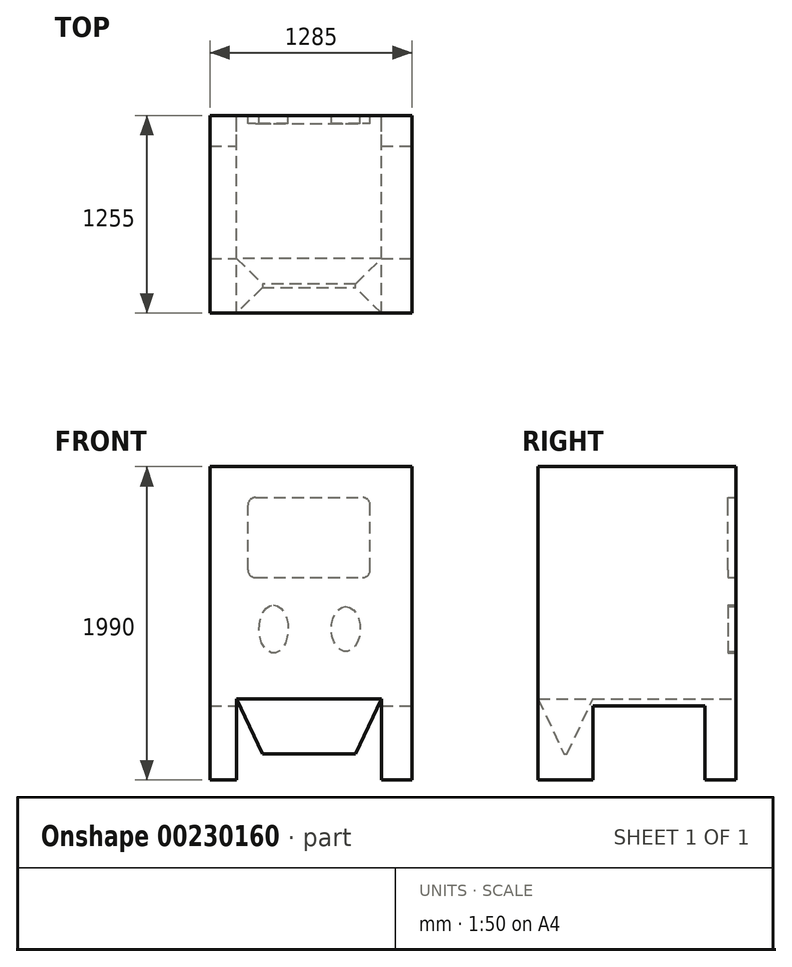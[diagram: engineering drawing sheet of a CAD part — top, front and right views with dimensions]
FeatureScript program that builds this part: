
annotation { "Feature Type Name" : "Feature", "Feature Type Description" : "" }
export const myFeature = defineFeature(function(context is Context, id is Id, definition is map)
    precondition{}
    {
        {
            var Q0;
            Q0=qCreatedBy(makeId("Top.planeOp"),FACE);
            var sketch = newSketch(context, id + "F0", { "sketchPlane" : qUnion([Q0])});
            skLineSegment(sketch, "E0.bottom", {"start": v(630, 615) * mm, "end": v(-630, 615) * mm});
            skLineSegment(sketch, "E0.top", {"start": v(630, -615) * mm, "end": v(-630, -615) * mm});
            skLineSegment(sketch, "E0.left", {"start": v(630, 615) * mm, "end": v(630, -615) * mm});
            skLineSegment(sketch, "E0.right", {"start": v(-630, 615) * mm, "end": v(-630, -615) * mm});
            skPoint(sketch, "E0.middle", {"position": v(0, 0) * mm});
            skSolve(sketch);
        }
        {
            var Q0;
            Q0=makeQuery(id+"F0.imprint","IMPRINT",FACE,{"disambiguationData":[TD([[makeQuery(id+"F0.imprint","IMPRINT",EDGE,{"derivedFrom":sQuery(id+"F0.wireOp",EDGE,"E0.bottom")}),1.0]])]});
            extrude(context, id + "F1", {"entities" : qUnion([Q0]), "depth" : 1990 * mm});
        }
        {
            var Q0;
            Q0=makeQuery(id+"F1.opExtrude","SWEPT_FACE",FACE,{"disambiguationData":[OSD([sQuery(id+"F0.wireOp",EDGE,"E0.bottom")])]});
            var sketch = newSketch(context, id + "F2", { "sketchPlane" : qUnion([Q0])});
            skLineSegment(sketch, "E1.bottom", {"start": v(338.4, 1285) * mm, "end": v(-338.4, 1285) * mm});
            skLineSegment(sketch, "E1.top", {"start": v(338.4, 1794.4) * mm, "end": v(-338.4, 1794.4) * mm});
            skLineSegment(sketch, "E1.left", {"start": v(388.4, 1335) * mm, "end": v(388.4, 1744.4) * mm});
            skLineSegment(sketch, "E1.right", {"start": v(-388.4, 1335) * mm, "end": v(-388.4, 1744.4) * mm});
            skPoint(sketch, "E1.middle", {"position": v(0, 1539.7) * mm});
            skPoint(sketch, "E2.visualSharp", {"position": v(-388.4, 1794.4) * mm});
            skArc(sketch, "E2.filletArc", {"start": v(-338.4, 1794.4) * mm, "mid": v(-373.76, 1779.76) * mm, "end": v(-388.4, 1744.4) * mm});
            skPoint(sketch, "E3.visualSharp", {"position": v(-388.4, 1285) * mm});
            skArc(sketch, "E3.filletArc", {"start": v(-388.4, 1335) * mm, "mid": v(-373.76, 1299.65) * mm, "end": v(-338.4, 1285) * mm});
            skPoint(sketch, "E4.visualSharp", {"position": v(388.4, 1285) * mm});
            skArc(sketch, "E4.filletArc", {"start": v(338.4, 1285) * mm, "mid": v(373.76, 1299.65) * mm, "end": v(388.4, 1335) * mm});
            skPoint(sketch, "E5.visualSharp", {"position": v(388.4, 1794.4) * mm});
            skArc(sketch, "E5.filletArc", {"start": v(388.4, 1744.4) * mm, "mid": v(373.76, 1779.76) * mm, "end": v(338.4, 1794.4) * mm});
            skEllipse(sketch, "E6", {"center": v(-233.06, 958.99) * mm, "majorRadius": 142.63 * mm, "minorRadius": 91.93 * mm, "majorAxis": v(0, 1)});
            skEllipse(sketch, "E7", {"center": v(225.4, 958.99) * mm, "majorRadius": 152.82 * mm, "minorRadius": 92.15 * mm, "majorAxis": v(0, 1)});
            skPoint(sketch, "E7.centerSnap0", {"position": v(-324.99, 958.99) * mm});
            skSolve(sketch);
        }
        {
            var Q0;
            Q0=makeQuery(id+"F2.imprint","IMPRINT",FACE,{"disambiguationData":[TD([[makeQuery(id+"F2.imprint","IMPRINT",EDGE,{"derivedFrom":sQuery(id+"F2.wireOp",EDGE,"E6")}),1.0]])]});
            var Q1;
            Q1=makeQuery(id+"F2.imprint","IMPRINT",FACE,{"disambiguationData":[TD([[makeQuery(id+"F2.imprint","IMPRINT",EDGE,{"derivedFrom":sQuery(id+"F2.wireOp",EDGE,"E7")}),1.0]])]});
            var Q2;
            Q2=makeQuery(id+"F2.imprint","IMPRINT",FACE,{"disambiguationData":[TD([[makeQuery(id+"F2.imprint","IMPRINT",EDGE,{"derivedFrom":sQuery(id+"F2.wireOp",EDGE,"E1.bottom")}),-1.0]])]});
            extrude(context, id + "F3", {"entities" : qUnion([Q0, Q1, Q2]), "operationType" : NewBodyOperationType.REMOVE, "oppositeDirection" : true, "depth" : 25 * mm});
        }
        {
            var Q0;
            Q0=makeQuery(id+"F1.opExtrude","SWEPT_FACE",FACE,{"disambiguationData":[OSD([sQuery(id+"F0.wireOp",EDGE,"E0.bottom")])]});
            extrude(context, id + "F4", {"entities" : qUnion([Q0]), "operationType" : NewBodyOperationType.ADD, "depth" : 25 * mm});
        }
        {
            var Q0;
            Q0=makeQuery(id+"F4.opExtrude","CAP_FACE",FACE,{"disambiguationData":[OSD([sQuery(id+"F0.wireOp",EDGE,"E0.bottom")])],"isStart":false});
            var sketch = newSketch(context, id + "F5", { "sketchPlane" : qUnion([Q0])});
            skLineSegment(sketch, "E8.bottom", {"start": v(459.56, 515.2) * mm, "end": v(-459.56, 515.2) * mm});
            skLineSegment(sketch, "E8.top", {"start": v(459.56, -515.2) * mm, "end": v(-459.56, -515.2) * mm});
            skLineSegment(sketch, "E8.left", {"start": v(459.56, 515.2) * mm, "end": v(459.56, -515.2) * mm});
            skLineSegment(sketch, "E8.right", {"start": v(-459.56, 515.2) * mm, "end": v(-459.56, -515.2) * mm});
            skPoint(sketch, "E8.middle", {"position": v(0, 0) * mm});
            skSolve(sketch);
        }
        {
            var Q0;
            Q0 = qSketchRegion(id + "F5", true);
            extrude(context, id + "F6", {"entities" : qUnion([Q0]), "operationType" : NewBodyOperationType.REMOVE, "oppositeDirection" : true, "depth" : 3660 * mm});
        }
        {
            var Q0;
            {var subQ0=sQuery(id+"F0.wireOp",EDGE,"E0.left");Q0=makeQuery(id+"F4.boolean.opBoolean","MERGE",FACE,{"derivedFrom":[makeQuery(id+"F1.opExtrude","SWEPT_FACE",FACE,{"disambiguationData":[OSD([subQ0])]}),makeQuery(id+"F4.opExtrude","SWEPT_FACE",FACE,{"disambiguationData":[OSD([sQuery(id+"F0.wireOp",EDGE,"E0.bottom"),subQ0])]})]});}
            extrude(context, id + "F7", {"entities" : qUnion([Q0]), "operationType" : NewBodyOperationType.ADD, "depth" : 25 * mm});
        }
        {
            var Q0;
            Q0=makeQuery(id+"F7.opExtrude","CAP_FACE",FACE,{"disambiguationData":[OSD([sQuery(id+"F0.wireOp",EDGE,"E0.bottom"),sQuery(id+"F0.wireOp",EDGE,"E0.left")])],"isStart":false});
            var sketch = newSketch(context, id + "F8", { "sketchPlane" : qUnion([Q0])});
            skLineSegment(sketch, "E9.bottom", {"start": v(-268.13, 471.42) * mm, "end": v(444.77, 471.42) * mm});
            skLineSegment(sketch, "E9.top", {"start": v(-268.13, -471.42) * mm, "end": v(444.77, -471.42) * mm});
            skLineSegment(sketch, "E9.left", {"start": v(-268.13, 471.42) * mm, "end": v(-268.13, -471.42) * mm});
            skLineSegment(sketch, "E9.right", {"start": v(444.77, 471.42) * mm, "end": v(444.77, -471.42) * mm});
            skPoint(sketch, "E9.middle", {"position": v(88.32, 0) * mm});
            skSolve(sketch);
        }
        {
            var Q0;
            Q0 = qSketchRegion(id + "F8", true);
            extrude(context, id + "F9", {"entities" : qUnion([Q0]), "operationType" : NewBodyOperationType.REMOVE, "oppositeDirection" : true, "depth" : 3440 * mm});
        }
        {
            var Q0;
            Q0=makeQuery(id+"F6.boolean.opBoolean","COPY",FACE,{"derivedFrom":makeQuery(id+"F6.opExtrude","SWEPT_FACE",FACE,{"disambiguationData":[OSD([sQuery(id+"F5.wireOp",EDGE,"E8.bottom")])]})});
            var sketch = newSketch(context, id + "F10", { "sketchPlane" : qUnion([Q0])});
            skLineSegment(sketch, "E10.bottom", {"start": v(459.56, 615) * mm, "end": v(-459.56, 615) * mm});
            skLineSegment(sketch, "E10.top", {"start": v(459.56, 267.35) * mm, "end": v(-459.56, 267.35) * mm});
            skLineSegment(sketch, "E10.left", {"start": v(459.56, 615) * mm, "end": v(459.56, 267.35) * mm});
            skLineSegment(sketch, "E10.right", {"start": v(-459.56, 615) * mm, "end": v(-459.56, 267.35) * mm});
            skSolve(sketch);
        }
        {
            var Q0;
            Q0=makeQuery(id+"F10.imprint","IMPRINT",FACE,{"disambiguationData":[TD([[makeQuery(id+"F10.imprint","IMPRINT",EDGE,{"derivedFrom":sQuery(id+"F10.wireOp",EDGE,"E10.bottom")}),1.0]])]});
            extrude(context, id + "F11", {"entities" : qUnion([Q0]), "operationType" : NewBodyOperationType.ADD, "depth" : 350 * mm, "hasDraft" : true, "draftAngle" : 25 * degree, "draftPullDirection" : true});
        }
    });
